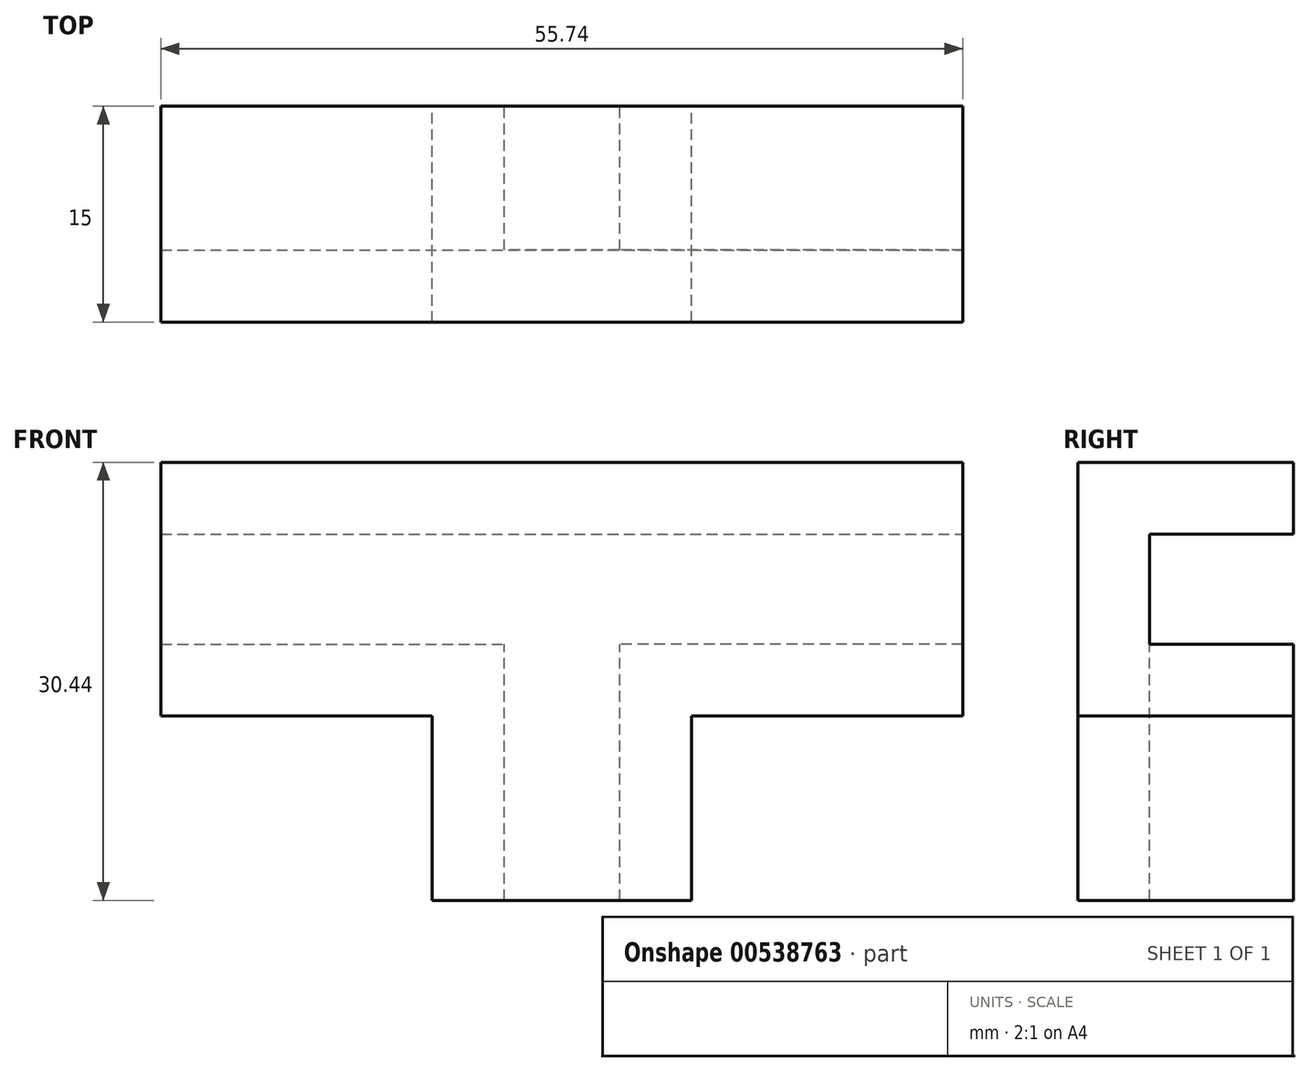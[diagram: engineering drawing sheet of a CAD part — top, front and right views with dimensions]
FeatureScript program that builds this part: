
annotation { "Feature Type Name" : "Feature", "Feature Type Description" : "" }
export const myFeature = defineFeature(function(context is Context, id is Id, definition is map)
    precondition{}
    {
        {
            var Q0;
            Q0=qCreatedBy(makeId("Front.planeOp"),FACE);
            var sketch = newSketch(context, id + "F0", { "sketchPlane" : qUnion([Q0])});
            skLineSegment(sketch, "E0", {"start": v(-27.87, 0) * mm, "end": v(0, 0) * mm, "construction": true});
            skLineSegment(sketch, "E1", {"start": v(0, -21.64) * mm, "end": v(-9.01, -21.64) * mm});
            skLineSegment(sketch, "E2", {"start": v(-9.01, -21.64) * mm, "end": v(-9.02, -8.83) * mm});
            skLineSegment(sketch, "E3", {"start": v(-9.01, -8.83) * mm, "end": v(-27.87, -8.83) * mm});
            skLineSegment(sketch, "E4", {"start": v(-27.87, -8.83) * mm, "end": v(-27.87, 0) * mm});
            skLineSegment(sketch, "E5", {"start": v(-4.02, -21.64) * mm, "end": v(-4.02, -3.83) * mm});
            skLineSegment(sketch, "E6", {"start": v(0, -21.64) * mm, "end": v(0, 0) * mm});
            skLineSegment(sketch, "E7", {"start": v(0, 0) * mm, "end": v(0, 8.8) * mm});
            skLineSegment(sketch, "E8", {"start": v(0, 8.8) * mm, "end": v(-27.87, 8.8) * mm});
            skLineSegment(sketch, "E9", {"start": v(-27.87, 8.8) * mm, "end": v(-27.87, 0) * mm});
            skLineSegment(sketch, "E10", {"start": v(-27.87, 3.8) * mm, "end": v(0, 3.8) * mm});
            skLineSegment(sketch, "E11", {"start": v(-27.87, -3.83) * mm, "end": v(-4.02, -3.83) * mm});
            skPoint(sketch, "E12.orphan", {"position": v(-4.02, -8.83) * mm});
            skPoint(sketch, "E13.orphan", {"position": v(0, -3.82) * mm});
            skSolve(sketch);
        }
        {
            var Q0;
            Q0 = qSketchRegion(id + "F0", true);
            extrude(context, id + "F1", {"entities" : qUnion([Q0]), "depth" : 15 * mm, "offsetDistance" : 25 * mm});
        }
        {
            var Q0;
            {var subQ1=sQuery(id+"F0.wireOp",EDGE,"E5");Q0=makeQuery(id+"F0.imprint","IMPRINT",FACE,{"disambiguationData":[TD([[makeQuery(id+"F0.imprint","IMPRINT",EDGE,{"derivedFrom":subQ1}),-1.0]])]});}
            extrude(context, id + "F2", {"entities" : qUnion([Q0]), "operationType" : NewBodyOperationType.REMOVE, "depth" : 10 * mm, "offsetDistance" : 25 * mm});
        }
        {
            var Q0;
            Q0=makeQuery(id+"F1.opExtrude","SWEPT_BODY",BODY,{"disambiguationData":[OSD([sQuery(id+"F0.wireOp",EDGE,"E1"),sQuery(id+"F0.wireOp",EDGE,"E2"),sQuery(id+"F0.wireOp",EDGE,"E3"),sQuery(id+"F0.wireOp",EDGE,"E4"),sQuery(id+"F0.wireOp",EDGE,"E6"),sQuery(id+"F0.wireOp",EDGE,"E7"),sQuery(id+"F0.wireOp",EDGE,"E8"),sQuery(id+"F0.wireOp",EDGE,"E9")])]});
            var Q1;
            Q1=qCreatedBy(makeId("Right.planeOp"),FACE);
            mirror(context, id + "F3", {"operationType" : NewBodyOperationType.ADD, "entities" : qUnion([Q0]), "mirrorPlane" : qUnion([Q1])});
        }
    });
